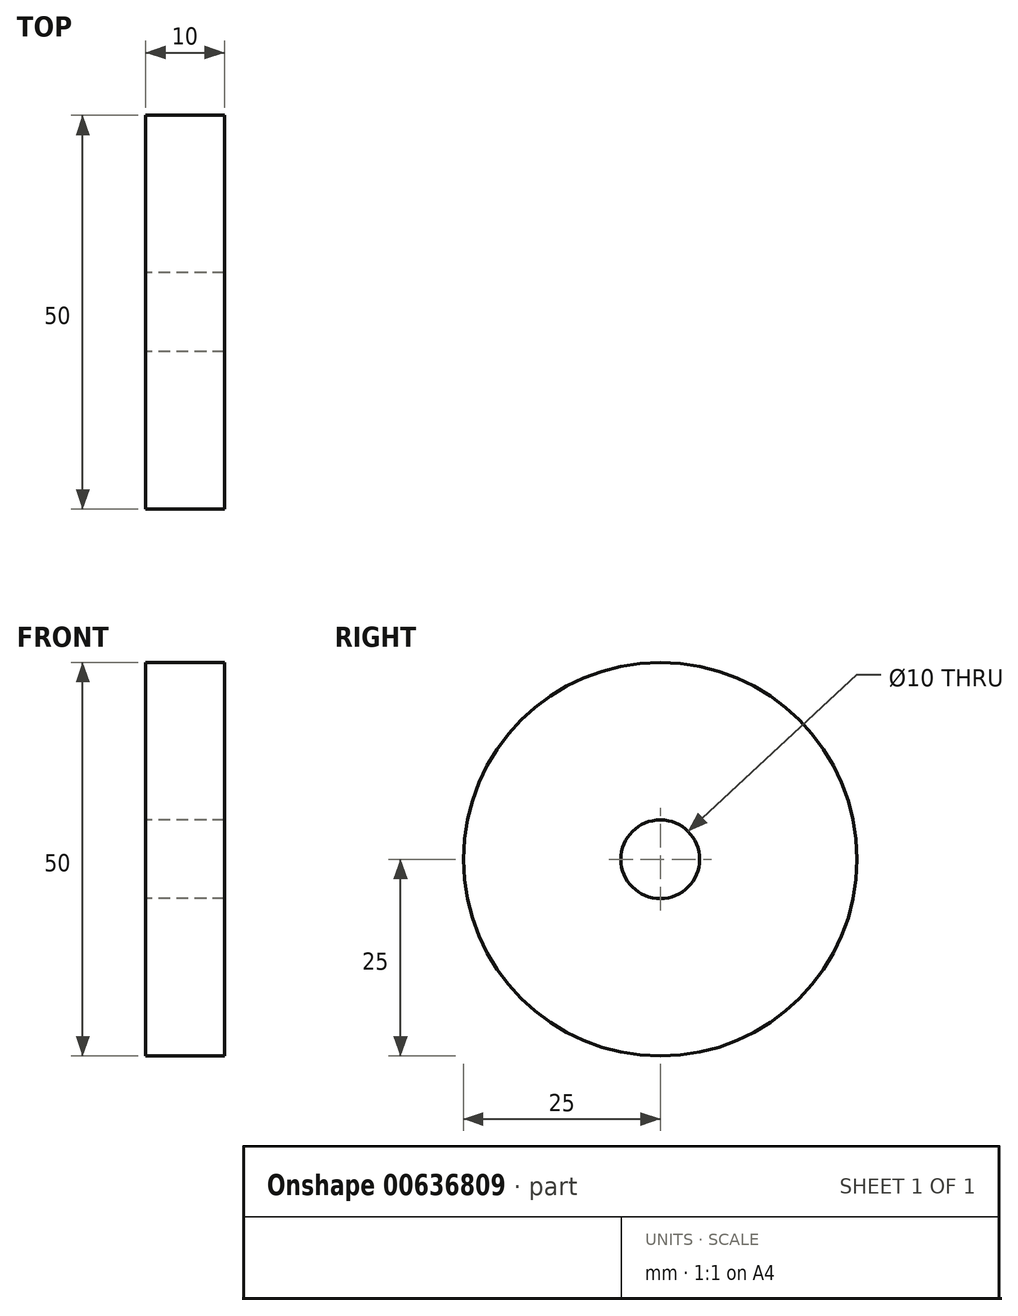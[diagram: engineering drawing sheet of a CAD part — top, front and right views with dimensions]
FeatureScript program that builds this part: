
annotation { "Feature Type Name" : "Feature", "Feature Type Description" : "" }
export const myFeature = defineFeature(function(context is Context, id is Id, definition is map)
    precondition{}
    {
        {
            var Q0;
            Q0=qCreatedBy(makeId("Right.planeOp"),FACE);
            var sketch = newSketch(context, id + "F0", { "sketchPlane" : qUnion([Q0])});
            skCircle(sketch, "E0.0", {"center": v(0, 0) * mm, "radius": 5 * mm});
            skCircle(sketch, "E1.0", {"center": v(0, 0) * mm, "radius": 25 * mm});
            skSolve(sketch);
        }
        {
            var Q0;
            Q0=makeQuery(id+"F0.imprint","IMPRINT",FACE,{"disambiguationData":[TD([[makeQuery(id+"F0.imprint","IMPRINT",EDGE,{"derivedFrom":sQuery(id+"F0.wireOp",EDGE,"E0.0")}),-1.0]])]});
            extrude(context, id + "F1", {"entities" : qUnion([Q0]), "depth" : 10 * mm, "offsetDistance" : 25 * mm});
        }
    });
